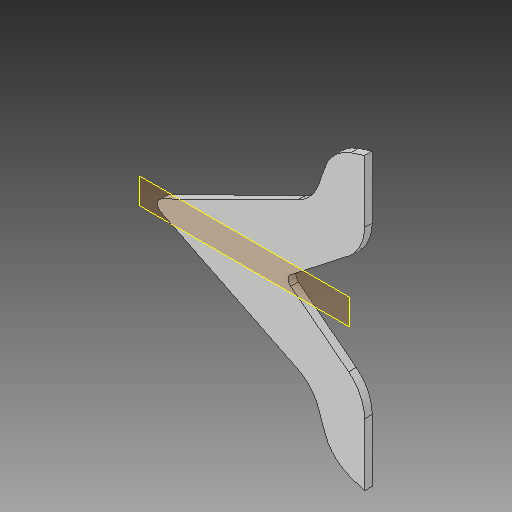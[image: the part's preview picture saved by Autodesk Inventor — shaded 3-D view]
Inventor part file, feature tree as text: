
AUTODESK INVENTOR PART (.ipt)
format: ipt  version: 2017 (Build 210142000, 142)  size: 101,376 bytes
history: native  units: in
note: dims shown in document units (in); Inventor stores cm internally (conversion verified against a paired STEP export)
features: other x3, sketch x1, plane x1
ambient origin geometry x8: Origin, YZ Plane, XZ Plane, XY Plane, X Axis, Y Axis, Z Axis, Center Point
bodies: Solid1 (feature_tree)
feature tree (5):
  other  "winglet.ipt"
  other  "Solid1::winglet.ipt"
  other  "TaggingFeature1"
  sketch  "Sketch1"  dims[d0=0.3937in]
  plane  "Work Plane1"
